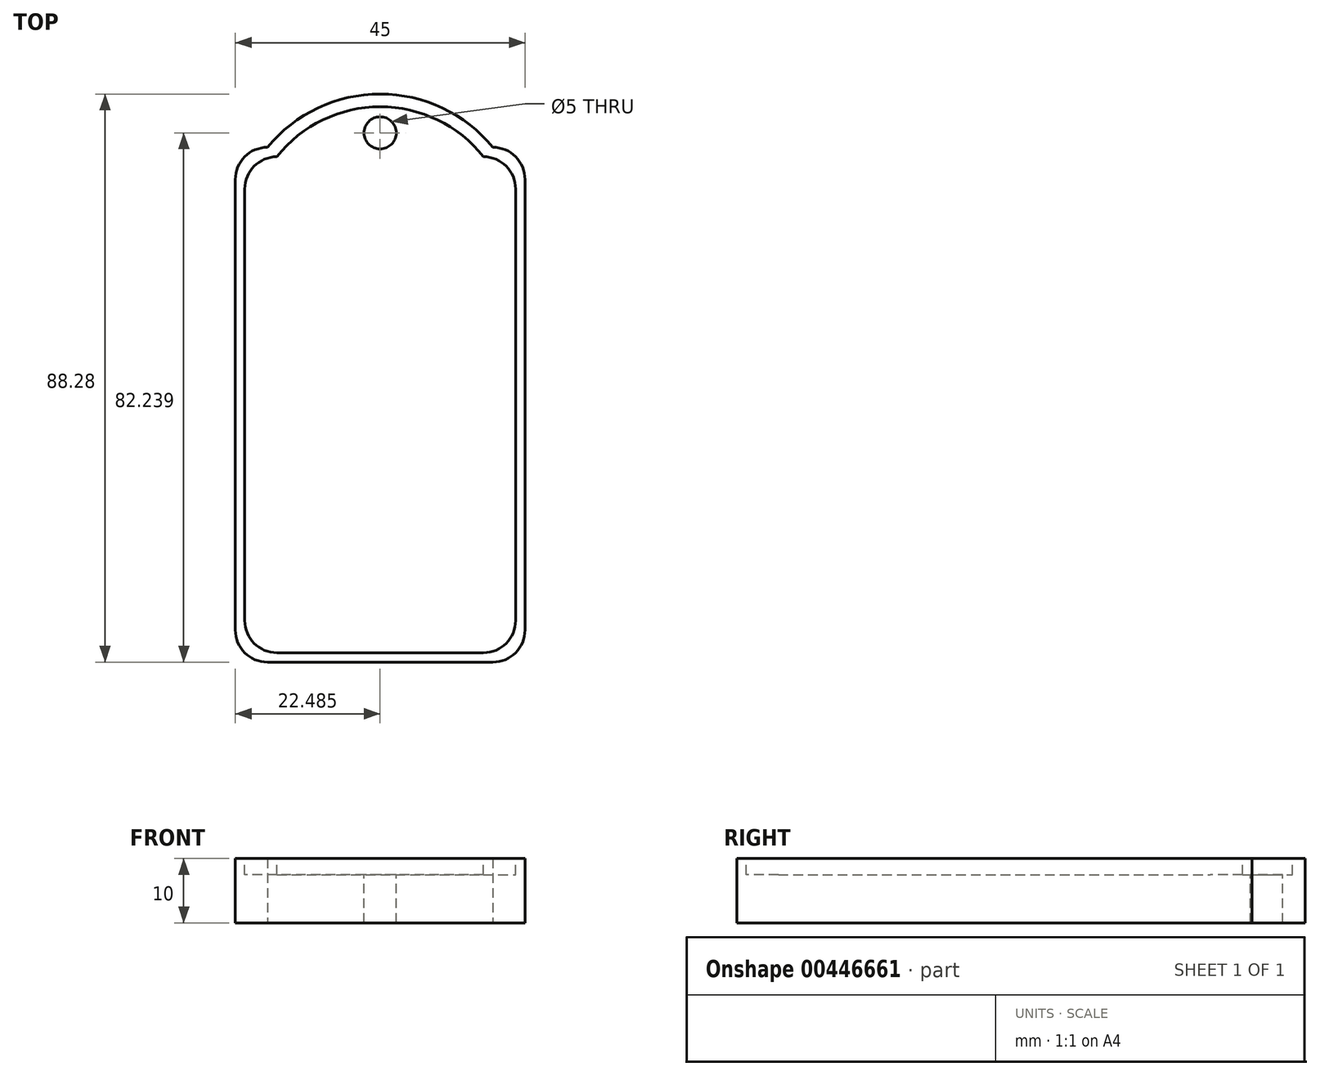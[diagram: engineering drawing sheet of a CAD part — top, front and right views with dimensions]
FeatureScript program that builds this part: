
annotation { "Feature Type Name" : "Feature", "Feature Type Description" : "" }
export const myFeature = defineFeature(function(context is Context, id is Id, definition is map)
    precondition{}
    {
        {
            var Q0;
            Q0=qCreatedBy(makeId("Top.planeOp"),FACE);
            var sketch = newSketch(context, id + "F0", { "sketchPlane" : qUnion([Q0])});
            skLineSegment(sketch, "E0.bottom", {"start": v(-1.9, -12.5) * mm, "end": v(33.1, -12.5) * mm});
            skLineSegment(sketch, "E0.top", {"start": v(-1.9, 67.5) * mm, "end": v(33.1, 67.5) * mm});
            skLineSegment(sketch, "E0.left", {"start": v(-6.9, -7.5) * mm, "end": v(-6.9, 62.5) * mm});
            skLineSegment(sketch, "E0.right", {"start": v(38.1, -7.5) * mm, "end": v(38.1, 62.5) * mm});
            skPoint(sketch, "E1.visualSharp", {"position": v(-6.9, 67.5) * mm});
            skArc(sketch, "E1.filletArc", {"start": v(-1.9, 67.5) * mm, "mid": v(-5.44, 66.03) * mm, "end": v(-6.9, 62.5) * mm});
            skPoint(sketch, "E2.visualSharp", {"position": v(38.1, 67.5) * mm});
            skArc(sketch, "E2.filletArc", {"start": v(38.1, 62.5) * mm, "mid": v(36.63, 66.03) * mm, "end": v(33.1, 67.5) * mm});
            skPoint(sketch, "E3.visualSharp", {"position": v(38.1, -12.5) * mm});
            skArc(sketch, "E3.filletArc", {"start": v(33.1, -12.5) * mm, "mid": v(36.63, -11.04) * mm, "end": v(38.1, -7.5) * mm});
            skPoint(sketch, "E4.visualSharp", {"position": v(-6.9, -12.5) * mm});
            skArc(sketch, "E4.filletArc", {"start": v(-6.9, -7.5) * mm, "mid": v(-5.44, -11.04) * mm, "end": v(-1.9, -12.5) * mm});
            skArc(sketch, "E5", {"start": v(33.1, 67.5) * mm, "mid": v(15.6, 75.78) * mm, "end": v(-1.9, 67.5) * mm});
            skSolve(sketch);
        }
        {
            var Q0;
            Q0=makeQuery(id+"F0.imprint","IMPRINT",FACE,{"disambiguationData":[TD([[makeQuery(id+"F0.imprint","IMPRINT",EDGE,{"derivedFrom":sQuery(id+"F0.wireOp",EDGE,"E0.top")}),1.0]])]});
            var Q1;
            Q1=makeQuery(id+"F0.imprint","IMPRINT",FACE,{"disambiguationData":[TD([[makeQuery(id+"F0.imprint","IMPRINT",EDGE,{"derivedFrom":sQuery(id+"F0.wireOp",EDGE,"E0.bottom")}),1.0]])]});
            extrude(context, id + "F1", {"entities" : qUnion([Q0, Q1]), "depth" : 10 * mm});
        }
        {
            var Q0;
            Q0=makeQuery(id+"F1.opExtrude","CAP_FACE",FACE,{"disambiguationData":[OSD([sQuery(id+"F0.wireOp",EDGE,"E0.bottom"),sQuery(id+"F0.wireOp",EDGE,"E0.left"),sQuery(id+"F0.wireOp",EDGE,"E0.right"),sQuery(id+"F0.wireOp",EDGE,"E1.filletArc"),sQuery(id+"F0.wireOp",EDGE,"E2.filletArc"),sQuery(id+"F0.wireOp",EDGE,"E3.filletArc"),sQuery(id+"F0.wireOp",EDGE,"E4.filletArc"),sQuery(id+"F0.wireOp",EDGE,"E5")])],"isStart":false});
            var sketch = newSketch(context, id + "F2", { "sketchPlane" : qUnion([Q0])});
            skLineSegment(sketch, "E6.bottom", {"start": v(-0.44, -11.04) * mm, "end": v(31.63, -11.04) * mm});
            skLineSegment(sketch, "E6.top", {"start": v(-0.44, 66.03) * mm, "end": v(31.63, 66.03) * mm});
            skLineSegment(sketch, "E6.left", {"start": v(-5.44, -6.04) * mm, "end": v(-5.44, 61.03) * mm});
            skLineSegment(sketch, "E6.right", {"start": v(36.63, -6.04) * mm, "end": v(36.63, 61.03) * mm});
            skPoint(sketch, "E7.visualSharp", {"position": v(-5.44, 66.03) * mm});
            skArc(sketch, "E7.filletArc", {"start": v(-0.44, 66.03) * mm, "mid": v(-3.98, 64.57) * mm, "end": v(-5.44, 61.03) * mm});
            skPoint(sketch, "E8.visualSharp", {"position": v(36.63, 66.03) * mm});
            skArc(sketch, "E8.filletArc", {"start": v(36.63, 61.03) * mm, "mid": v(35.17, 64.57) * mm, "end": v(31.63, 66.03) * mm});
            skPoint(sketch, "E9.visualSharp", {"position": v(36.63, -11.04) * mm});
            skArc(sketch, "E9.filletArc", {"start": v(31.63, -11.04) * mm, "mid": v(35.17, -9.57) * mm, "end": v(36.63, -6.04) * mm});
            skPoint(sketch, "E10.visualSharp", {"position": v(-5.44, -11.04) * mm});
            skArc(sketch, "E10.filletArc", {"start": v(-5.44, -6.04) * mm, "mid": v(-3.98, -9.57) * mm, "end": v(-0.44, -11.04) * mm});
            skArc(sketch, "E11", {"start": v(31.63, 66.03) * mm, "mid": v(15.6, 73.8) * mm, "end": v(-0.44, 66.03) * mm});
            skCircle(sketch, "E12", {"center": v(15.58, 69.74) * mm, "radius": 2.5 * mm});
            skSolve(sketch);
        }
        {
            var Q0;
            Q0=makeQuery(id+"F2.imprint","IMPRINT",FACE,{"disambiguationData":[TD([[makeQuery(id+"F2.imprint","IMPRINT",EDGE,{"derivedFrom":sQuery(id+"F2.wireOp",EDGE,"E6.top")}),1.0]])]});
            var Q1;
            Q1=makeQuery(id+"F2.imprint","IMPRINT",FACE,{"disambiguationData":[TD([[makeQuery(id+"F2.imprint","IMPRINT",EDGE,{"derivedFrom":sQuery(id+"F2.wireOp",EDGE,"E6.bottom")}),1.0]])]});
            extrude(context, id + "F3", {"entities" : qUnion([Q0, Q1]), "operationType" : NewBodyOperationType.REMOVE, "oppositeDirection" : true, "depth" : 2.5 * mm});
        }
        {
            var Q0;
            Q0=makeQuery(id+"F3.boolean.opBoolean","SPLIT",FACE,{"disambiguationData":[TD([makeQuery(id+"F3.opExtrude","SWEPT_FACE",FACE,{"disambiguationData":[OSD([sQuery(id+"F2.wireOp",EDGE,"E12")])]})])],"derivedFrom":makeQuery(id+"F1.opExtrude","CAP_FACE",FACE,{"disambiguationData":[OSD([sQuery(id+"F0.wireOp",EDGE,"E0.bottom"),sQuery(id+"F0.wireOp",EDGE,"E0.left"),sQuery(id+"F0.wireOp",EDGE,"E0.right"),sQuery(id+"F0.wireOp",EDGE,"E1.filletArc"),sQuery(id+"F0.wireOp",EDGE,"E2.filletArc"),sQuery(id+"F0.wireOp",EDGE,"E3.filletArc"),sQuery(id+"F0.wireOp",EDGE,"E4.filletArc"),sQuery(id+"F0.wireOp",EDGE,"E5")])],"isStart":false})});
            extrude(context, id + "F4", {"entities" : qUnion([Q0]), "operationType" : NewBodyOperationType.REMOVE, "oppositeDirection" : true, "depth" : 40.9 * mm});
        }
    });
